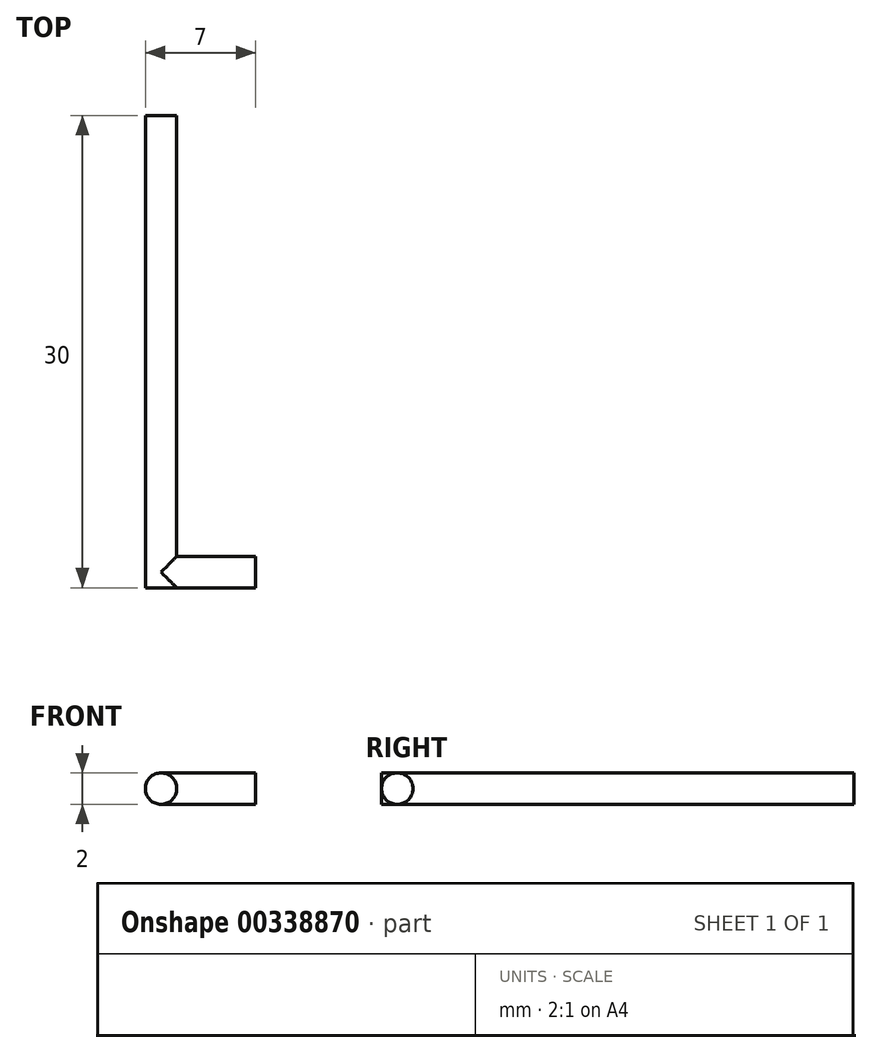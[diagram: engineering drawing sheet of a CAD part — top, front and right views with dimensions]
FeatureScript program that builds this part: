
annotation { "Feature Type Name" : "Feature", "Feature Type Description" : "" }
export const myFeature = defineFeature(function(context is Context, id is Id, definition is map)
    precondition{}
    {
        {
            var Q0;
            Q0=qCreatedBy(makeId("Front.planeOp"),FACE);
            var sketch = newSketch(context, id + "F0", { "sketchPlane" : qUnion([Q0])});
            skCircle(sketch, "E0", {"center": v(0, 0) * mm, "radius": 1 * mm});
            skSolve(sketch);
        }
        {
            var Q0;
            Q0 = qSketchRegion(id + "F0", true);
            extrude(context, id + "F1", {"entities" : qUnion([Q0]), "depth" : 30 * mm});
        }
        {
            var Q0;
            Q0=qCreatedBy(makeId("Right.planeOp"),FACE);
            var sketch = newSketch(context, id + "F2", { "sketchPlane" : qUnion([Q0])});
            skCircle(sketch, "E1", {"center": v(-29, 0) * mm, "radius": 1 * mm});
            skSolve(sketch);
        }
        {
            var Q0;
            Q0 = qSketchRegion(id + "F2", true);
            extrude(context, id + "F3", {"entities" : qUnion([Q0]), "operationType" : NewBodyOperationType.ADD, "depth" : 6 * mm});
        }
    });
